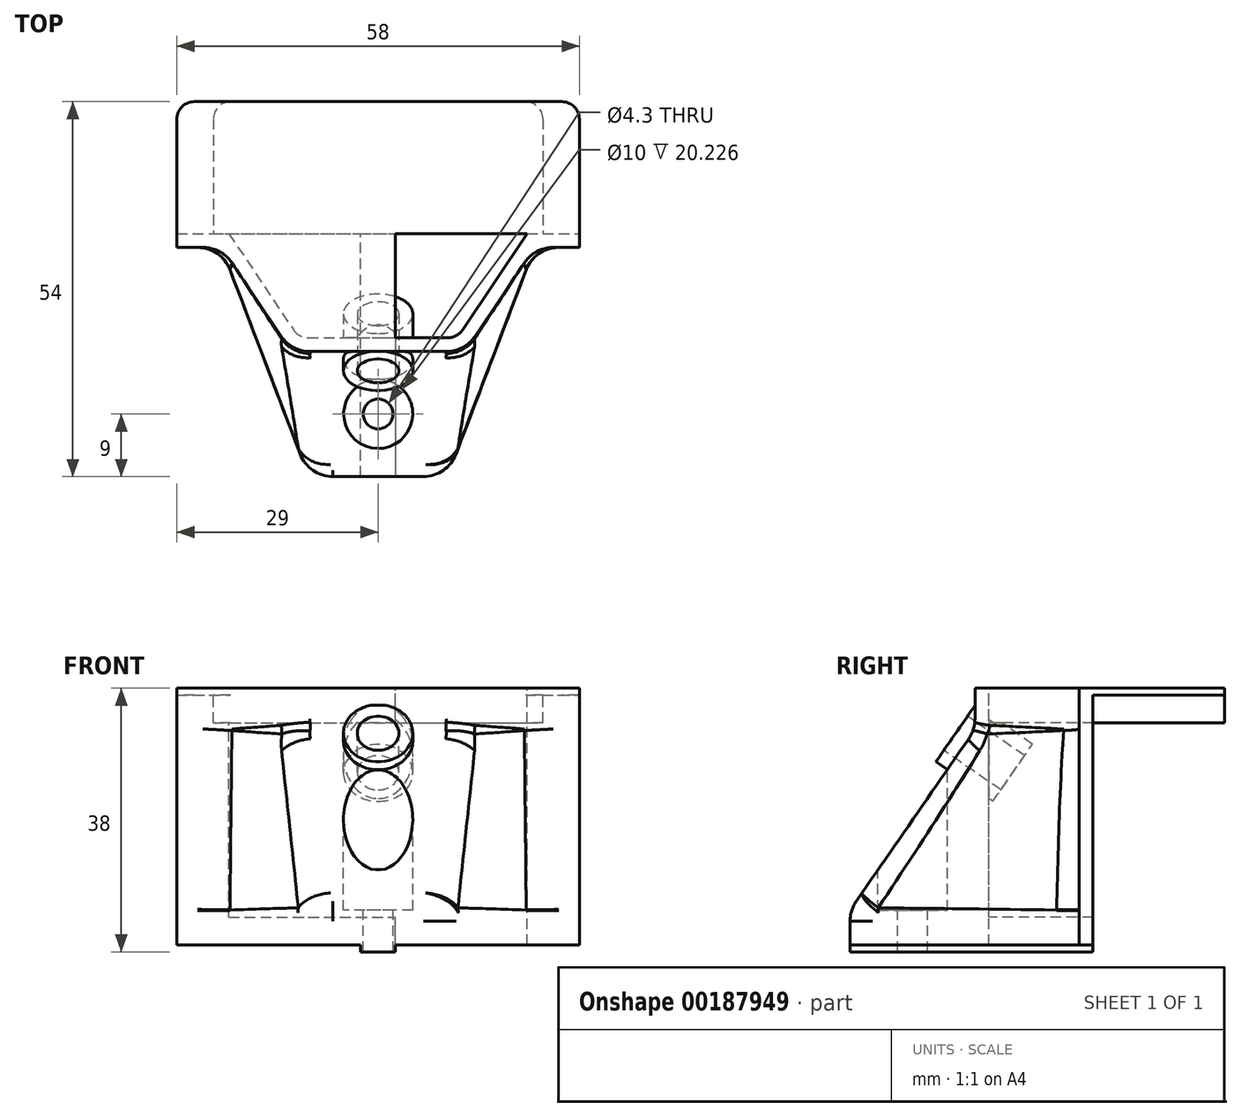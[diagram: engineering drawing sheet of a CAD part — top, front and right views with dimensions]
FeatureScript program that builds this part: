
annotation { "Feature Type Name" : "Feature", "Feature Type Description" : "" }
export const myFeature = defineFeature(function(context is Context, id is Id, definition is map)
    precondition{}
    {
        {
            var Q0;
            Q0=qCreatedBy(makeId("Top.planeOp"),FACE);
            var sketch = newSketch(context, id + "F0", { "sketchPlane" : qUnion([Q0])});
            skLineSegment(sketch, "E0", {"start": v(0, 38.36) * mm, "end": v(0, -38.36) * mm, "construction": true});
            skLineSegment(sketch, "E1.bottom", {"start": v(-29, 19) * mm, "end": v(29, 19) * mm});
            skLineSegment(sketch, "E1.top", {"start": v(-29, 0) * mm, "end": v(29, 0) * mm});
            skLineSegment(sketch, "E1.left", {"start": v(-29, 19) * mm, "end": v(-29, 0) * mm});
            skLineSegment(sketch, "E1.right", {"start": v(29, 19) * mm, "end": v(29, 0) * mm});
            skLineSegment(sketch, "E2", {"start": v(-23.75, 19) * mm, "end": v(-23.75, 0) * mm});
            skLineSegment(sketch, "E3", {"start": v(23.75, 19) * mm, "end": v(23.75, 0) * mm});
            skLineSegment(sketch, "E4.left", {"start": v(-29, 0) * mm, "end": v(-29, -2) * mm});
            skLineSegment(sketch, "E4.right", {"start": v(29, 0) * mm, "end": v(29, -2) * mm});
            skLineSegment(sketch, "E5", {"start": v(-10, -35) * mm, "end": v(10, -35) * mm});
            skLineSegment(sketch, "E6", {"start": v(-21.5, 0) * mm, "end": v(-11.43, -15) * mm});
            skLineSegment(sketch, "E7", {"start": v(11.43, -15) * mm, "end": v(21.5, 0) * mm});
            skLineSegment(sketch, "E8", {"start": v(21.5, 0) * mm, "end": v(11.43, -15) * mm});
            skLineSegment(sketch, "E9", {"start": v(-11.43, -15) * mm, "end": v(11.43, -15) * mm});
            skLineSegment(sketch, "E10", {"start": v(-29, -2) * mm, "end": v(-22.57, -2) * mm});
            skLineSegment(sketch, "E11", {"start": v(29, -2) * mm, "end": v(22.57, -2) * mm});
            skLineSegment(sketch, "E12", {"start": v(-22.57, -2) * mm, "end": v(-12.5, -17) * mm});
            skLineSegment(sketch, "E13", {"start": v(-12.5, -17) * mm, "end": v(12.5, -17) * mm});
            skLineSegment(sketch, "E14", {"start": v(12.5, -17) * mm, "end": v(22.57, -2) * mm});
            skCircle(sketch, "E15", {"center": v(0, -26) * mm, "radius": 2.15 * mm});
            skLineSegment(sketch, "E16", {"start": v(-2.5, -35) * mm, "end": v(-2.5, 0) * mm});
            skLineSegment(sketch, "E17", {"start": v(2.5, 0) * mm, "end": v(2.5, -35) * mm});
            skLineSegment(sketch, "E18", {"start": v(-22.57, -2) * mm, "end": v(-10, -35) * mm});
            skLineSegment(sketch, "E19", {"start": v(22.57, -2) * mm, "end": v(10, -35) * mm});
            skLineSegment(sketch, "E20", {"start": v(12.5, -17) * mm, "end": v(-12.5, -17) * mm});
            skSolve(sketch);
        }
        {
            var Q0;
            {var subQ1=sQuery(id+"F0.wireOp",EDGE,"E2");Q0=makeQuery(id+"F0.imprint","IMPRINT",FACE,{"disambiguationData":[TD([[makeQuery(id+"F0.imprint","IMPRINT",EDGE,{"derivedFrom":subQ1}),1.0]])]});}
            var Q1;
            {var subQ0=sQuery(id+"F0.wireOp",EDGE,"E1.left");Q1=makeQuery(id+"F0.imprint","IMPRINT",FACE,{"disambiguationData":[TD([[makeQuery(id+"F0.imprint","IMPRINT",EDGE,{"derivedFrom":subQ0}),1.0]])]});}
            var Q2;
            {var subQ0=sQuery(id+"F0.wireOp",EDGE,"E1.right");Q2=makeQuery(id+"F0.imprint","IMPRINT",FACE,{"disambiguationData":[TD([[makeQuery(id+"F0.imprint","IMPRINT",EDGE,{"derivedFrom":subQ0}),-1.0]])]});}
            var Q3;
            {var subQ5=sQuery(id+"F0.wireOp",EDGE,"E4.left");Q3=makeQuery(id+"F0.imprint","IMPRINT",FACE,{"disambiguationData":[TD([[makeQuery(id+"F0.imprint","IMPRINT",EDGE,{"derivedFrom":subQ5}),1.0]])]});}
            var Q4;
            {var subQ0=sQuery(id+"F0.wireOp",EDGE,"E6");Q4=makeQuery(id+"F0.imprint","IMPRINT",FACE,{"disambiguationData":[TD([[makeQuery(id+"F0.imprint","IMPRINT",EDGE,{"derivedFrom":subQ0}),1.0]])]});}
            var Q5;
            {var subQ0=sQuery(id+"F0.wireOp",EDGE,"E16");var subQ1=sQuery(id+"F0.wireOp",EDGE,"E1.top");var subQ2=makeQuery(id+"F0.imprint","INTERSECT",VERTEX,{"derivedFrom":[subQ1,subQ0]});Q5=makeQuery(id+"F0.imprint","IMPRINT",FACE,{"disambiguationData":[TD([[makeQuery(id+"F0.imprint","IMPRINT",EDGE,{"disambiguationData":[TD([[subQ2,-1.0]])],"derivedFrom":subQ1}),-1.0]])]});}
            var Q6;
            {var subQ0=sQuery(id+"F0.wireOp",EDGE,"E8");Q6=makeQuery(id+"F0.imprint","IMPRINT",FACE,{"disambiguationData":[TD([[makeQuery(id+"F0.imprint","IMPRINT",EDGE,{"derivedFrom":subQ0}),-1.0]])]});}
            var Q7;
            {var subQ1=sQuery(id+"F0.wireOp",EDGE,"E4.right");Q7=makeQuery(id+"F0.imprint","IMPRINT",FACE,{"disambiguationData":[TD([[makeQuery(id+"F0.imprint","IMPRINT",EDGE,{"derivedFrom":subQ1}),-1.0]])]});}
            var Q8;
            {var subQ0=sQuery(id+"F0.wireOp",EDGE,"E16");var subQ1=sQuery(id+"F0.wireOp",EDGE,"E9");var subQ2=makeQuery(id+"F0.imprint","INTERSECT",VERTEX,{"derivedFrom":[subQ1,subQ0]});Q8=makeQuery(id+"F0.imprint","IMPRINT",FACE,{"disambiguationData":[TD([[makeQuery(id+"F0.imprint","IMPRINT",EDGE,{"disambiguationData":[TD([[subQ2,-1.0]])],"derivedFrom":subQ1}),-1.0]])]});}
            var Q9;
            {var subQ7=sQuery(id+"F0.wireOp",EDGE,"CKm9zJXj-dWNc-FXDy-1bbl-akqoD4z67Doo");Q9=makeQuery(id+"F0.imprint","IMPRINT",FACE,{"disambiguationData":[TD([[makeQuery(id+"F0.imprint","IMPRINT",EDGE,{"derivedFrom":subQ7}),-1.0]])]});}
            var Q10;
            {var subQ6=sQuery(id+"F0.wireOp",EDGE,"E6");Q10=makeQuery(id+"F0.imprint","IMPRINT",FACE,{"disambiguationData":[TD([[makeQuery(id+"F0.imprint","IMPRINT",EDGE,{"derivedFrom":subQ6}),-1.0]])]});}
            var Q11;
            {var subQ5=sQuery(id+"F0.wireOp",EDGE,"E8");Q11=makeQuery(id+"F0.imprint","IMPRINT",FACE,{"disambiguationData":[TD([[makeQuery(id+"F0.imprint","IMPRINT",EDGE,{"derivedFrom":subQ5}),1.0]])]});}
            var Q12;
            {var subQ5=sQuery(id+"F0.wireOp",EDGE,"ojLpUpTn-VgTE-xdOx-HgIy-6l8KoOz5zoZN");Q12=makeQuery(id+"F0.imprint","IMPRINT",FACE,{"disambiguationData":[TD([[makeQuery(id+"F0.imprint","IMPRINT",EDGE,{"derivedFrom":subQ5}),1.0]])]});}
            extrude(context, id + "F1", {"entities" : qUnion([Q0, Q1, Q2, Q3, Q4, Q5, Q6, Q7, Q8, Q9, Q10, Q11, Q12]), "oppositeDirection" : true, "depth" : 1 * mm});
        }
        {
            var Q0;
            {var subQ1=sQuery(id+"F0.wireOp",EDGE,"E2");Q0=makeQuery(id+"F0.imprint","IMPRINT",FACE,{"disambiguationData":[TD([[makeQuery(id+"F0.imprint","IMPRINT",EDGE,{"derivedFrom":subQ1}),1.0]])]});}
            var Q1;
            {var subQ5=sQuery(id+"F0.wireOp",EDGE,"E4.left");Q1=makeQuery(id+"F0.imprint","IMPRINT",FACE,{"disambiguationData":[TD([[makeQuery(id+"F0.imprint","IMPRINT",EDGE,{"derivedFrom":subQ5}),1.0]])]});}
            var Q2;
            {var subQ1=sQuery(id+"F0.wireOp",EDGE,"E4.right");Q2=makeQuery(id+"F0.imprint","IMPRINT",FACE,{"disambiguationData":[TD([[makeQuery(id+"F0.imprint","IMPRINT",EDGE,{"derivedFrom":subQ1}),-1.0]])]});}
            var Q3;
            {var subQ0=sQuery(id+"F0.wireOp",EDGE,"E16");var subQ1=sQuery(id+"F0.wireOp",EDGE,"E9");var subQ2=makeQuery(id+"F0.imprint","INTERSECT",VERTEX,{"derivedFrom":[subQ1,subQ0]});Q3=makeQuery(id+"F0.imprint","IMPRINT",FACE,{"disambiguationData":[TD([[makeQuery(id+"F0.imprint","IMPRINT",EDGE,{"disambiguationData":[TD([[subQ2,-1.0]])],"derivedFrom":subQ1}),-1.0]])]});}
            var Q4;
            {var subQ0=sQuery(id+"F0.wireOp",EDGE,"E8");Q4=makeQuery(id+"F0.imprint","IMPRINT",FACE,{"disambiguationData":[TD([[makeQuery(id+"F0.imprint","IMPRINT",EDGE,{"derivedFrom":subQ0}),-1.0]])]});}
            var Q5;
            {var subQ0=sQuery(id+"F0.wireOp",EDGE,"E16");var subQ1=sQuery(id+"F0.wireOp",EDGE,"E1.top");var subQ2=makeQuery(id+"F0.imprint","INTERSECT",VERTEX,{"derivedFrom":[subQ1,subQ0]});Q5=makeQuery(id+"F0.imprint","IMPRINT",FACE,{"disambiguationData":[TD([[makeQuery(id+"F0.imprint","IMPRINT",EDGE,{"disambiguationData":[TD([[subQ2,-1.0]])],"derivedFrom":subQ1}),-1.0]])]});}
            var Q6;
            {var subQ0=sQuery(id+"F0.wireOp",EDGE,"E6");Q6=makeQuery(id+"F0.imprint","IMPRINT",FACE,{"disambiguationData":[TD([[makeQuery(id+"F0.imprint","IMPRINT",EDGE,{"derivedFrom":subQ0}),1.0]])]});}
            var Q7;
            {var subQ7=sQuery(id+"F0.wireOp",EDGE,"CKm9zJXj-dWNc-FXDy-1bbl-akqoD4z67Doo");Q7=makeQuery(id+"F0.imprint","IMPRINT",FACE,{"disambiguationData":[TD([[makeQuery(id+"F0.imprint","IMPRINT",EDGE,{"derivedFrom":subQ7}),-1.0]])]});}
            var Q8;
            {var subQ6=sQuery(id+"F0.wireOp",EDGE,"E6");Q8=makeQuery(id+"F0.imprint","IMPRINT",FACE,{"disambiguationData":[TD([[makeQuery(id+"F0.imprint","IMPRINT",EDGE,{"derivedFrom":subQ6}),-1.0]])]});}
            var Q9;
            {var subQ5=sQuery(id+"F0.wireOp",EDGE,"E8");Q9=makeQuery(id+"F0.imprint","IMPRINT",FACE,{"disambiguationData":[TD([[makeQuery(id+"F0.imprint","IMPRINT",EDGE,{"derivedFrom":subQ5}),1.0]])]});}
            var Q10;
            {var subQ5=sQuery(id+"F0.wireOp",EDGE,"ojLpUpTn-VgTE-xdOx-HgIy-6l8KoOz5zoZN");Q10=makeQuery(id+"F0.imprint","IMPRINT",FACE,{"disambiguationData":[TD([[makeQuery(id+"F0.imprint","IMPRINT",EDGE,{"derivedFrom":subQ5}),1.0]])]});}
            extrude(context, id + "F2", {"entities" : qUnion([Q0, Q1, Q2, Q3, Q4, Q5, Q6, Q7, Q8, Q9, Q10]), "operationType" : NewBodyOperationType.ADD, "oppositeDirection" : true, "depth" : 5 * mm, "hasSecondDirection" : true, "secondDirectionOppositeDirection" : true, "secondDirectionDepth" : 1 * mm});
        }
        {
            var Q0;
            {var subQ0=sQuery(id+"F0.wireOp",EDGE,"E16");var subQ1=sQuery(id+"F0.wireOp",EDGE,"Ah3oLFyD-nscL-xTTO-zcLj-mXIpSbA0FtKH");var subQ2=makeQuery(id+"F0.imprint","INTERSECT",VERTEX,{"disambiguationData":[OD(0.0)],"derivedFrom":[subQ1,subQ0]});Q0=makeQuery(id+"F0.imprint","IMPRINT",FACE,{"disambiguationData":[TD([[makeQuery(id+"F0.imprint","IMPRINT",EDGE,{"disambiguationData":[TD([[subQ2,-1.0]])],"derivedFrom":subQ1}),1.0]])]});}
            var Q1;
            {var subQ0=sQuery(id+"F0.wireOp",EDGE,"E16");var subQ1=sQuery(id+"F0.wireOp",EDGE,"E5");var subQ2=makeQuery(id+"F0.imprint","INTERSECT",VERTEX,{"derivedFrom":[subQ1,subQ0]});Q1=makeQuery(id+"F0.imprint","IMPRINT",FACE,{"disambiguationData":[TD([[makeQuery(id+"F0.imprint","IMPRINT",EDGE,{"disambiguationData":[TD([[subQ2,-1.0]])],"derivedFrom":subQ1}),1.0]])]});}
            var Q2;
            Q2=makeQuery(id+"F0.imprint","IMPRINT",FACE,{"disambiguationData":[TD([[makeQuery(id+"F0.imprint","IMPRINT",EDGE,{"derivedFrom":sQuery(id+"F0.wireOp",EDGE,"E15")}),-1.0]])]});
            var Q3;
            {var subQ5=sQuery(id+"F0.wireOp",EDGE,"gXHjxx1o-LBkh-gjxu-DR8X-Vu5xXttBdvo7");Q3=makeQuery(id+"F0.imprint","IMPRINT",FACE,{"disambiguationData":[TD([[makeQuery(id+"F0.imprint","IMPRINT",EDGE,{"derivedFrom":subQ5}),-1.0]])]});}
            var Q4;
            {var subQ0=sQuery(id+"F0.wireOp",EDGE,"E17");var subQ1=sQuery(id+"F0.wireOp",EDGE,"Ah3oLFyD-nscL-xTTO-zcLj-mXIpSbA0FtKH");var subQ2=makeQuery(id+"F0.imprint","INTERSECT",VERTEX,{"disambiguationData":[OD(0.0)],"derivedFrom":[subQ1,subQ0]});Q4=makeQuery(id+"F0.imprint","IMPRINT",FACE,{"disambiguationData":[TD([[makeQuery(id+"F0.imprint","IMPRINT",EDGE,{"disambiguationData":[TD([[subQ2,1.0]])],"derivedFrom":subQ1}),1.0]])]});}
            var Q5;
            {var subQ5=sQuery(id+"F0.wireOp",EDGE,"E4.left");Q5=makeQuery(id+"F0.imprint","IMPRINT",FACE,{"disambiguationData":[TD([[makeQuery(id+"F0.imprint","IMPRINT",EDGE,{"derivedFrom":subQ5}),1.0]])]});}
            var Q6;
            {var subQ0=sQuery(id+"F0.wireOp",EDGE,"E6");Q6=makeQuery(id+"F0.imprint","IMPRINT",FACE,{"disambiguationData":[TD([[makeQuery(id+"F0.imprint","IMPRINT",EDGE,{"derivedFrom":subQ0}),1.0]])]});}
            var Q7;
            {var subQ0=sQuery(id+"F0.wireOp",EDGE,"E8");Q7=makeQuery(id+"F0.imprint","IMPRINT",FACE,{"disambiguationData":[TD([[makeQuery(id+"F0.imprint","IMPRINT",EDGE,{"derivedFrom":subQ0}),-1.0]])]});}
            var Q8;
            {var subQ1=sQuery(id+"F0.wireOp",EDGE,"E4.right");Q8=makeQuery(id+"F0.imprint","IMPRINT",FACE,{"disambiguationData":[TD([[makeQuery(id+"F0.imprint","IMPRINT",EDGE,{"derivedFrom":subQ1}),-1.0]])]});}
            var Q9;
            {var subQ0=sQuery(id+"F0.wireOp",EDGE,"E16");var subQ1=sQuery(id+"F0.wireOp",EDGE,"E1.top");var subQ2=makeQuery(id+"F0.imprint","INTERSECT",VERTEX,{"derivedFrom":[subQ1,subQ0]});Q9=makeQuery(id+"F0.imprint","IMPRINT",FACE,{"disambiguationData":[TD([[makeQuery(id+"F0.imprint","IMPRINT",EDGE,{"disambiguationData":[TD([[subQ2,-1.0]])],"derivedFrom":subQ1}),-1.0]])]});}
            var Q10;
            {var subQ0=sQuery(id+"F0.wireOp",EDGE,"E16");var subQ1=sQuery(id+"F0.wireOp",EDGE,"E13");var subQ2=makeQuery(id+"F0.imprint","INTERSECT",VERTEX,{"derivedFrom":[subQ1,subQ0]});Q10=makeQuery(id+"F0.imprint","IMPRINT",FACE,{"disambiguationData":[TD([[makeQuery(id+"F0.imprint","IMPRINT",EDGE,{"disambiguationData":[TD([[subQ2,-1.0]])],"derivedFrom":subQ1}),-1.0]])]});}
            var Q11;
            {var subQ7=sQuery(id+"F0.wireOp",EDGE,"CKm9zJXj-dWNc-FXDy-1bbl-akqoD4z67Doo");Q11=makeQuery(id+"F0.imprint","IMPRINT",FACE,{"disambiguationData":[TD([[makeQuery(id+"F0.imprint","IMPRINT",EDGE,{"derivedFrom":subQ7}),-1.0]])]});}
            var Q12;
            {var subQ6=sQuery(id+"F0.wireOp",EDGE,"E6");Q12=makeQuery(id+"F0.imprint","IMPRINT",FACE,{"disambiguationData":[TD([[makeQuery(id+"F0.imprint","IMPRINT",EDGE,{"derivedFrom":subQ6}),-1.0]])]});}
            var Q13;
            {var subQ0=sQuery(id+"F0.wireOp",EDGE,"E16");var subQ1=sQuery(id+"F0.wireOp",EDGE,"E9");var subQ2=makeQuery(id+"F0.imprint","INTERSECT",VERTEX,{"derivedFrom":[subQ1,subQ0]});Q13=makeQuery(id+"F0.imprint","IMPRINT",FACE,{"disambiguationData":[TD([[makeQuery(id+"F0.imprint","IMPRINT",EDGE,{"disambiguationData":[TD([[subQ2,-1.0]])],"derivedFrom":subQ1}),-1.0]])]});}
            var Q14;
            {var subQ5=sQuery(id+"F0.wireOp",EDGE,"E8");Q14=makeQuery(id+"F0.imprint","IMPRINT",FACE,{"disambiguationData":[TD([[makeQuery(id+"F0.imprint","IMPRINT",EDGE,{"derivedFrom":subQ5}),1.0]])]});}
            var Q15;
            {var subQ1=sQuery(id+"F0.wireOp",EDGE,"E12");var subQ3=sQuery(id+"F0.wireOp",EDGE,"0NOjFGGp-TMjN-rOI9-zP1e-SuJYmJxnuehr");var subQ4=makeQuery(id+"F0.imprint","INTERSECT",VERTEX,{"derivedFrom":[subQ1,subQ3]});Q15=makeQuery(id+"F0.imprint","IMPRINT",FACE,{"disambiguationData":[TD([[makeQuery(id+"F0.imprint","IMPRINT",EDGE,{"disambiguationData":[TD([[subQ4,1.0]])],"derivedFrom":subQ1}),-1.0]])]});}
            var Q16;
            {var subQ5=sQuery(id+"F0.wireOp",EDGE,"E13");var subQ7=sQuery(id+"F0.wireOp",EDGE,"E12");var subQ8=makeQuery(id+"F0.imprint","INTERSECT",VERTEX,{"derivedFrom":[subQ7,subQ5]});Q16=makeQuery(id+"F0.imprint","IMPRINT",FACE,{"disambiguationData":[TD([[makeQuery(id+"F0.imprint","IMPRINT",EDGE,{"disambiguationData":[TD([[subQ8,1.0]])],"derivedFrom":subQ7}),-1.0]])]});}
            var Q17;
            {var subQ3=sQuery(id+"F0.wireOp",EDGE,"Ah3oLFyD-nscL-xTTO-zcLj-mXIpSbA0FtKH");var subQ9=sQuery(id+"F0.wireOp",EDGE,"E20");var subQ10=makeQuery(id+"F0.imprint","INTERSECT",VERTEX,{"disambiguationData":[OD(0.0)],"derivedFrom":[subQ3,subQ9]});Q17=makeQuery(id+"F0.imprint","IMPRINT",FACE,{"disambiguationData":[TD([[makeQuery(id+"F0.imprint","IMPRINT",EDGE,{"disambiguationData":[TD([[subQ10,-1.0]])],"derivedFrom":subQ3}),-1.0]])]});}
            var Q18;
            {var subQ0=sQuery(id+"F0.wireOp",EDGE,"E16");var subQ1=sQuery(id+"F0.wireOp",EDGE,"Ah3oLFyD-nscL-xTTO-zcLj-mXIpSbA0FtKH");var subQ2=makeQuery(id+"F0.imprint","INTERSECT",VERTEX,{"disambiguationData":[OD(1.0)],"derivedFrom":[subQ1,subQ0]});Q18=makeQuery(id+"F0.imprint","IMPRINT",FACE,{"disambiguationData":[TD([[makeQuery(id+"F0.imprint","IMPRINT",EDGE,{"disambiguationData":[TD([[subQ2,-1.0]])],"derivedFrom":subQ1}),1.0]])]});}
            var Q19;
            {var subQ0=sQuery(id+"F0.wireOp",EDGE,"E20");var subQ1=sQuery(id+"F0.wireOp",EDGE,"Ah3oLFyD-nscL-xTTO-zcLj-mXIpSbA0FtKH");var subQ2=makeQuery(id+"F0.imprint","INTERSECT",VERTEX,{"disambiguationData":[OD(0.0)],"derivedFrom":[subQ1,subQ0]});Q19=makeQuery(id+"F0.imprint","IMPRINT",FACE,{"disambiguationData":[TD([[makeQuery(id+"F0.imprint","IMPRINT",EDGE,{"disambiguationData":[TD([[subQ2,-1.0]])],"derivedFrom":subQ1}),1.0]])]});}
            var Q20;
            {var subQ0=sQuery(id+"F0.wireOp",EDGE,"E17");var subQ1=sQuery(id+"F0.wireOp",EDGE,"Ah3oLFyD-nscL-xTTO-zcLj-mXIpSbA0FtKH");var subQ2=makeQuery(id+"F0.imprint","INTERSECT",VERTEX,{"disambiguationData":[OD(1.0)],"derivedFrom":[subQ1,subQ0]});Q20=makeQuery(id+"F0.imprint","IMPRINT",FACE,{"disambiguationData":[TD([[makeQuery(id+"F0.imprint","IMPRINT",EDGE,{"disambiguationData":[TD([[subQ2,-1.0]])],"derivedFrom":subQ1}),1.0]])]});}
            var Q21;
            {var subQ5=sQuery(id+"F0.wireOp",EDGE,"E17");var subQ7=sQuery(id+"F0.wireOp",EDGE,"Ah3oLFyD-nscL-xTTO-zcLj-mXIpSbA0FtKH");var subQ8=makeQuery(id+"F0.imprint","INTERSECT",VERTEX,{"disambiguationData":[OD(1.0)],"derivedFrom":[subQ7,subQ5]});Q21=makeQuery(id+"F0.imprint","IMPRINT",FACE,{"disambiguationData":[TD([[makeQuery(id+"F0.imprint","IMPRINT",EDGE,{"disambiguationData":[TD([[subQ8,-1.0]])],"derivedFrom":subQ7}),-1.0]])]});}
            var Q22;
            {var subQ1=sQuery(id+"F0.wireOp",EDGE,"E13");var subQ9=sQuery(id+"F0.wireOp",EDGE,"E14");var subQ11=makeQuery(id+"F0.imprint","INTERSECT",VERTEX,{"derivedFrom":[subQ1,subQ9]});Q22=makeQuery(id+"F0.imprint","IMPRINT",FACE,{"disambiguationData":[TD([[makeQuery(id+"F0.imprint","IMPRINT",EDGE,{"disambiguationData":[TD([[subQ11,1.0]])],"derivedFrom":subQ1}),-1.0]])]});}
            var Q23;
            {var subQ1=sQuery(id+"F0.wireOp",EDGE,"E14");var subQ3=sQuery(id+"F0.wireOp",EDGE,"tBigfjPw-6Owl-bpDE-Yp1M-dKvZaqhM0liG");var subQ4=makeQuery(id+"F0.imprint","INTERSECT",VERTEX,{"derivedFrom":[subQ1,subQ3]});Q23=makeQuery(id+"F0.imprint","IMPRINT",FACE,{"disambiguationData":[TD([[makeQuery(id+"F0.imprint","IMPRINT",EDGE,{"disambiguationData":[TD([[subQ4,-1.0]])],"derivedFrom":subQ1}),-1.0]])]});}
            var Q24;
            {var subQ5=sQuery(id+"F0.wireOp",EDGE,"ojLpUpTn-VgTE-xdOx-HgIy-6l8KoOz5zoZN");Q24=makeQuery(id+"F0.imprint","IMPRINT",FACE,{"disambiguationData":[TD([[makeQuery(id+"F0.imprint","IMPRINT",EDGE,{"derivedFrom":subQ5}),1.0]])]});}
            var Q25;
            Q25=makeQuery(id+"F0.imprint","IMPRINT",FACE,{"disambiguationData":[TD([[makeQuery(id+"F0.imprint","IMPRINT",EDGE,{"derivedFrom":sQuery(id+"F0.wireOp",EDGE,"E15")}),1.0]])]});
            extrude(context, id + "F3", {"entities" : qUnion([Q0, Q1, Q2, Q3, Q4, Q5, Q6, Q7, Q8, Q9, Q10, Q11, Q12, Q13, Q14, Q15, Q16, Q17, Q18, Q19, Q20, Q21, Q22, Q23, Q24, Q25]), "operationType" : NewBodyOperationType.ADD, "oppositeDirection" : true, "depth" : 37 * mm, "hasSecondDirection" : true, "secondDirectionOppositeDirection" : true, "secondDirectionDepth" : 33 * mm});
        }
        {
            var Q0;
            {var subQ5=sQuery(id+"F0.wireOp",EDGE,"gXHjxx1o-LBkh-gjxu-DR8X-Vu5xXttBdvo7");Q0=makeQuery(id+"F0.imprint","IMPRINT",FACE,{"disambiguationData":[TD([[makeQuery(id+"F0.imprint","IMPRINT",EDGE,{"derivedFrom":subQ5}),-1.0]])]});}
            var Q1;
            {var subQ0=sQuery(id+"F0.wireOp",EDGE,"E16");var subQ1=sQuery(id+"F0.wireOp",EDGE,"E5");var subQ2=makeQuery(id+"F0.imprint","INTERSECT",VERTEX,{"derivedFrom":[subQ1,subQ0]});Q1=makeQuery(id+"F0.imprint","IMPRINT",FACE,{"disambiguationData":[TD([[makeQuery(id+"F0.imprint","IMPRINT",EDGE,{"disambiguationData":[TD([[subQ2,-1.0]])],"derivedFrom":subQ1}),1.0]])]});}
            var Q2;
            {var subQ0=sQuery(id+"F0.wireOp",EDGE,"E16");var subQ1=sQuery(id+"F0.wireOp",EDGE,"Ah3oLFyD-nscL-xTTO-zcLj-mXIpSbA0FtKH");var subQ2=makeQuery(id+"F0.imprint","INTERSECT",VERTEX,{"disambiguationData":[OD(1.0)],"derivedFrom":[subQ1,subQ0]});Q2=makeQuery(id+"F0.imprint","IMPRINT",FACE,{"disambiguationData":[TD([[makeQuery(id+"F0.imprint","IMPRINT",EDGE,{"disambiguationData":[TD([[subQ2,-1.0]])],"derivedFrom":subQ1}),1.0]])]});}
            var Q3;
            Q3=makeQuery(id+"F0.imprint","IMPRINT",FACE,{"disambiguationData":[TD([[makeQuery(id+"F0.imprint","IMPRINT",EDGE,{"derivedFrom":sQuery(id+"F0.wireOp",EDGE,"E15")}),-1.0]])]});
            var Q4;
            {var subQ0=sQuery(id+"F0.wireOp",EDGE,"E16");var subQ1=sQuery(id+"F0.wireOp",EDGE,"E13");var subQ2=makeQuery(id+"F0.imprint","INTERSECT",VERTEX,{"derivedFrom":[subQ1,subQ0]});Q4=makeQuery(id+"F0.imprint","IMPRINT",FACE,{"disambiguationData":[TD([[makeQuery(id+"F0.imprint","IMPRINT",EDGE,{"disambiguationData":[TD([[subQ2,-1.0]])],"derivedFrom":subQ1}),-1.0]])]});}
            var Q5;
            {var subQ0=sQuery(id+"F0.wireOp",EDGE,"E16");var subQ1=sQuery(id+"F0.wireOp",EDGE,"E9");var subQ2=makeQuery(id+"F0.imprint","INTERSECT",VERTEX,{"derivedFrom":[subQ1,subQ0]});Q5=makeQuery(id+"F0.imprint","IMPRINT",FACE,{"disambiguationData":[TD([[makeQuery(id+"F0.imprint","IMPRINT",EDGE,{"disambiguationData":[TD([[subQ2,-1.0]])],"derivedFrom":subQ1}),-1.0]])]});}
            var Q6;
            {var subQ0=sQuery(id+"F0.wireOp",EDGE,"E16");var subQ1=sQuery(id+"F0.wireOp",EDGE,"E1.top");var subQ2=makeQuery(id+"F0.imprint","INTERSECT",VERTEX,{"derivedFrom":[subQ1,subQ0]});Q6=makeQuery(id+"F0.imprint","IMPRINT",FACE,{"disambiguationData":[TD([[makeQuery(id+"F0.imprint","IMPRINT",EDGE,{"disambiguationData":[TD([[subQ2,-1.0]])],"derivedFrom":subQ1}),-1.0]])]});}
            var Q7;
            {var subQ0=sQuery(id+"F0.wireOp",EDGE,"E16");var subQ1=sQuery(id+"F0.wireOp",EDGE,"Ah3oLFyD-nscL-xTTO-zcLj-mXIpSbA0FtKH");var subQ2=makeQuery(id+"F0.imprint","INTERSECT",VERTEX,{"disambiguationData":[OD(0.0)],"derivedFrom":[subQ1,subQ0]});Q7=makeQuery(id+"F0.imprint","IMPRINT",FACE,{"disambiguationData":[TD([[makeQuery(id+"F0.imprint","IMPRINT",EDGE,{"disambiguationData":[TD([[subQ2,1.0]])],"derivedFrom":subQ1}),-1.0]])]});}
            var Q8;
            Q8=makeQuery(id+"F0.imprint","IMPRINT",FACE,{"disambiguationData":[TD([[makeQuery(id+"F0.imprint","IMPRINT",EDGE,{"derivedFrom":sQuery(id+"F0.wireOp",EDGE,"E15")}),1.0]])]});
            extrude(context, id + "F4", {"entities" : qUnion([Q0, Q1, Q2, Q3, Q4, Q5, Q6, Q7, Q8]), "operationType" : NewBodyOperationType.ADD, "oppositeDirection" : true, "depth" : 38 * mm, "hasSecondDirection" : true, "secondDirectionOppositeDirection" : true, "secondDirectionDepth" : 37 * mm});
        }
        {
            var Q0;
            {var subQ0=sQuery(id+"F0.wireOp",EDGE,"E4.left");Q0=makeQuery(id+"F0.imprint","IMPRINT",FACE,{"disambiguationData":[TD([[makeQuery(id+"F0.imprint","IMPRINT",EDGE,{"derivedFrom":subQ0}),1.0]])]});}
            var Q1;
            {var subQ7=sQuery(id+"F0.wireOp",EDGE,"CKm9zJXj-dWNc-FXDy-1bbl-akqoD4z67Doo");Q1=makeQuery(id+"F0.imprint","IMPRINT",FACE,{"disambiguationData":[TD([[makeQuery(id+"F0.imprint","IMPRINT",EDGE,{"derivedFrom":subQ7}),-1.0]])]});}
            var Q2;
            {var subQ6=sQuery(id+"F0.wireOp",EDGE,"E6");Q2=makeQuery(id+"F0.imprint","IMPRINT",FACE,{"disambiguationData":[TD([[makeQuery(id+"F0.imprint","IMPRINT",EDGE,{"derivedFrom":subQ6}),-1.0]])]});}
            var Q3;
            {var subQ0=sQuery(id+"F0.wireOp",EDGE,"E16");var subQ1=sQuery(id+"F0.wireOp",EDGE,"E9");var subQ2=makeQuery(id+"F0.imprint","INTERSECT",VERTEX,{"derivedFrom":[subQ1,subQ0]});Q3=makeQuery(id+"F0.imprint","IMPRINT",FACE,{"disambiguationData":[TD([[makeQuery(id+"F0.imprint","IMPRINT",EDGE,{"disambiguationData":[TD([[subQ2,-1.0]])],"derivedFrom":subQ1}),-1.0]])]});}
            var Q4;
            {var subQ5=sQuery(id+"F0.wireOp",EDGE,"E8");Q4=makeQuery(id+"F0.imprint","IMPRINT",FACE,{"disambiguationData":[TD([[makeQuery(id+"F0.imprint","IMPRINT",EDGE,{"derivedFrom":subQ5}),1.0]])]});}
            var Q5;
            {var subQ5=sQuery(id+"F0.wireOp",EDGE,"ojLpUpTn-VgTE-xdOx-HgIy-6l8KoOz5zoZN");Q5=makeQuery(id+"F0.imprint","IMPRINT",FACE,{"disambiguationData":[TD([[makeQuery(id+"F0.imprint","IMPRINT",EDGE,{"derivedFrom":subQ5}),1.0]])]});}
            var Q6;
            {var subQ0=sQuery(id+"F0.wireOp",EDGE,"E4.right");Q6=makeQuery(id+"F0.imprint","IMPRINT",FACE,{"disambiguationData":[TD([[makeQuery(id+"F0.imprint","IMPRINT",EDGE,{"derivedFrom":subQ0}),-1.0]])]});}
            extrude(context, id + "F5", {"entities" : qUnion([Q0, Q1, Q2, Q3, Q4, Q5, Q6]), "operationType" : NewBodyOperationType.ADD, "oppositeDirection" : true, "depth" : 6 * mm, "hasSecondDirection" : true, "secondDirectionOppositeDirection" : true, "secondDirectionDepth" : 5 * mm});
        }
        {
            var Q0;
            {var subQ0=sQuery(id+"F0.wireOp",EDGE,"E4.left");Q0=makeQuery(id+"F0.imprint","IMPRINT",FACE,{"disambiguationData":[TD([[makeQuery(id+"F0.imprint","IMPRINT",EDGE,{"derivedFrom":subQ0}),1.0]])]});}
            var Q1;
            {var subQ3=sQuery(id+"F0.wireOp",EDGE,"Ah3oLFyD-nscL-xTTO-zcLj-mXIpSbA0FtKH");var subQ9=sQuery(id+"F0.wireOp",EDGE,"E20");var subQ10=makeQuery(id+"F0.imprint","INTERSECT",VERTEX,{"disambiguationData":[OD(0.0)],"derivedFrom":[subQ3,subQ9]});Q1=makeQuery(id+"F0.imprint","IMPRINT",FACE,{"disambiguationData":[TD([[makeQuery(id+"F0.imprint","IMPRINT",EDGE,{"disambiguationData":[TD([[subQ10,-1.0]])],"derivedFrom":subQ3}),-1.0]])]});}
            var Q2;
            {var subQ0=sQuery(id+"F0.wireOp",EDGE,"E16");var subQ1=sQuery(id+"F0.wireOp",EDGE,"E5");var subQ2=makeQuery(id+"F0.imprint","INTERSECT",VERTEX,{"derivedFrom":[subQ1,subQ0]});Q2=makeQuery(id+"F0.imprint","IMPRINT",FACE,{"disambiguationData":[TD([[makeQuery(id+"F0.imprint","IMPRINT",EDGE,{"disambiguationData":[TD([[subQ2,-1.0]])],"derivedFrom":subQ1}),1.0]])]});}
            var Q3;
            {var subQ5=sQuery(id+"F0.wireOp",EDGE,"E17");var subQ7=sQuery(id+"F0.wireOp",EDGE,"Ah3oLFyD-nscL-xTTO-zcLj-mXIpSbA0FtKH");var subQ8=makeQuery(id+"F0.imprint","INTERSECT",VERTEX,{"disambiguationData":[OD(1.0)],"derivedFrom":[subQ7,subQ5]});Q3=makeQuery(id+"F0.imprint","IMPRINT",FACE,{"disambiguationData":[TD([[makeQuery(id+"F0.imprint","IMPRINT",EDGE,{"disambiguationData":[TD([[subQ8,-1.0]])],"derivedFrom":subQ7}),-1.0]])]});}
            var Q4;
            {var subQ0=sQuery(id+"F0.wireOp",EDGE,"E4.right");Q4=makeQuery(id+"F0.imprint","IMPRINT",FACE,{"disambiguationData":[TD([[makeQuery(id+"F0.imprint","IMPRINT",EDGE,{"derivedFrom":subQ0}),-1.0]])]});}
            var Q5;
            {var subQ0=sQuery(id+"F0.wireOp",EDGE,"E16");var subQ1=sQuery(id+"F0.wireOp",EDGE,"Ah3oLFyD-nscL-xTTO-zcLj-mXIpSbA0FtKH");var subQ2=makeQuery(id+"F0.imprint","INTERSECT",VERTEX,{"disambiguationData":[OD(1.0)],"derivedFrom":[subQ1,subQ0]});Q5=makeQuery(id+"F0.imprint","IMPRINT",FACE,{"disambiguationData":[TD([[makeQuery(id+"F0.imprint","IMPRINT",EDGE,{"disambiguationData":[TD([[subQ2,-1.0]])],"derivedFrom":subQ1}),1.0]])]});}
            var Q6;
            {var subQ0=sQuery(id+"F0.wireOp",EDGE,"E20");var subQ1=sQuery(id+"F0.wireOp",EDGE,"Ah3oLFyD-nscL-xTTO-zcLj-mXIpSbA0FtKH");var subQ2=makeQuery(id+"F0.imprint","INTERSECT",VERTEX,{"disambiguationData":[OD(0.0)],"derivedFrom":[subQ1,subQ0]});Q6=makeQuery(id+"F0.imprint","IMPRINT",FACE,{"disambiguationData":[TD([[makeQuery(id+"F0.imprint","IMPRINT",EDGE,{"disambiguationData":[TD([[subQ2,-1.0]])],"derivedFrom":subQ1}),1.0]])]});}
            var Q7;
            {var subQ0=sQuery(id+"F0.wireOp",EDGE,"E17");var subQ1=sQuery(id+"F0.wireOp",EDGE,"Ah3oLFyD-nscL-xTTO-zcLj-mXIpSbA0FtKH");var subQ2=makeQuery(id+"F0.imprint","INTERSECT",VERTEX,{"disambiguationData":[OD(1.0)],"derivedFrom":[subQ1,subQ0]});Q7=makeQuery(id+"F0.imprint","IMPRINT",FACE,{"disambiguationData":[TD([[makeQuery(id+"F0.imprint","IMPRINT",EDGE,{"disambiguationData":[TD([[subQ2,-1.0]])],"derivedFrom":subQ1}),1.0]])]});}
            var Q8;
            {var subQ7=sQuery(id+"F0.wireOp",EDGE,"CKm9zJXj-dWNc-FXDy-1bbl-akqoD4z67Doo");Q8=makeQuery(id+"F0.imprint","IMPRINT",FACE,{"disambiguationData":[TD([[makeQuery(id+"F0.imprint","IMPRINT",EDGE,{"derivedFrom":subQ7}),-1.0]])]});}
            var Q9;
            {var subQ1=sQuery(id+"F0.wireOp",EDGE,"E12");var subQ3=sQuery(id+"F0.wireOp",EDGE,"0NOjFGGp-TMjN-rOI9-zP1e-SuJYmJxnuehr");var subQ4=makeQuery(id+"F0.imprint","INTERSECT",VERTEX,{"derivedFrom":[subQ1,subQ3]});Q9=makeQuery(id+"F0.imprint","IMPRINT",FACE,{"disambiguationData":[TD([[makeQuery(id+"F0.imprint","IMPRINT",EDGE,{"disambiguationData":[TD([[subQ4,1.0]])],"derivedFrom":subQ1}),-1.0]])]});}
            var Q10;
            {var subQ5=sQuery(id+"F0.wireOp",EDGE,"ojLpUpTn-VgTE-xdOx-HgIy-6l8KoOz5zoZN");Q10=makeQuery(id+"F0.imprint","IMPRINT",FACE,{"disambiguationData":[TD([[makeQuery(id+"F0.imprint","IMPRINT",EDGE,{"derivedFrom":subQ5}),1.0]])]});}
            var Q11;
            {var subQ1=sQuery(id+"F0.wireOp",EDGE,"E14");var subQ3=sQuery(id+"F0.wireOp",EDGE,"tBigfjPw-6Owl-bpDE-Yp1M-dKvZaqhM0liG");var subQ4=makeQuery(id+"F0.imprint","INTERSECT",VERTEX,{"derivedFrom":[subQ1,subQ3]});Q11=makeQuery(id+"F0.imprint","IMPRINT",FACE,{"disambiguationData":[TD([[makeQuery(id+"F0.imprint","IMPRINT",EDGE,{"disambiguationData":[TD([[subQ4,-1.0]])],"derivedFrom":subQ1}),-1.0]])]});}
            var Q12;
            {var subQ0=sQuery(id+"F0.wireOp",EDGE,"E16");var subQ1=sQuery(id+"F0.wireOp",EDGE,"E9");var subQ2=makeQuery(id+"F0.imprint","INTERSECT",VERTEX,{"derivedFrom":[subQ1,subQ0]});Q12=makeQuery(id+"F0.imprint","IMPRINT",FACE,{"disambiguationData":[TD([[makeQuery(id+"F0.imprint","IMPRINT",EDGE,{"disambiguationData":[TD([[subQ2,-1.0]])],"derivedFrom":subQ1}),-1.0]])]});}
            var Q13;
            Q13=makeQuery(id+"F0.imprint","IMPRINT",FACE,{"disambiguationData":[TD([[makeQuery(id+"F0.imprint","IMPRINT",EDGE,{"derivedFrom":sQuery(id+"F0.wireOp",EDGE,"E15")}),1.0]])]});
            extrude(context, id + "F6", {"entities" : qUnion([Q0, Q1, Q2, Q3, Q4, Q5, Q6, Q7, Q8, Q9, Q10, Q11, Q12, Q13]), "operationType" : NewBodyOperationType.ADD, "oppositeDirection" : true, "depth" : 33 * mm, "hasSecondDirection" : true, "secondDirectionOppositeDirection" : true, "secondDirectionDepth" : 32 * mm});
        }
        {
            var Q0;
            Q0=makeQuery(id+"F6.opExtrude","CAP_FACE",FACE,{"disambiguationData":[OSD([sQuery(id+"F0.wireOp",EDGE,"E1.top"),sQuery(id+"F0.wireOp",EDGE,"E4.left"),sQuery(id+"F0.wireOp",EDGE,"E4.right"),sQuery(id+"F0.wireOp",EDGE,"E5"),sQuery(id+"F0.wireOp",EDGE,"E10"),sQuery(id+"F0.wireOp",EDGE,"E11"),sQuery(id+"F0.wireOp",EDGE,"E18"),sQuery(id+"F0.wireOp",EDGE,"E19"),sQuery(id+"F0.wireOp",EDGE,"tBigfjPw-6Owl-bpDE-Yp1M-dKvZaqhM0liG"),sQuery(id+"F0.wireOp",EDGE,"E20"),sQuery(id+"F0.wireOp",EDGE,"0NOjFGGp-TMjN-rOI9-zP1e-SuJYmJxnuehr")])],"isStart":true});
            var Q1;
            Q1=makeQuery(id+"F5.opExtrude","CAP_FACE",FACE,{"disambiguationData":[OSD([sQuery(id+"F0.wireOp",EDGE,"E1.top"),sQuery(id+"F0.wireOp",EDGE,"E4.left"),sQuery(id+"F0.wireOp",EDGE,"E4.right"),sQuery(id+"F0.wireOp",EDGE,"E6"),sQuery(id+"F0.wireOp",EDGE,"E8"),sQuery(id+"F0.wireOp",EDGE,"E9"),sQuery(id+"F0.wireOp",EDGE,"E10"),sQuery(id+"F0.wireOp",EDGE,"E11"),sQuery(id+"F0.wireOp",EDGE,"E12"),sQuery(id+"F0.wireOp",EDGE,"E13"),sQuery(id+"F0.wireOp",EDGE,"E14")])],"isStart":false});
            loft(context, id + "F7", {"sheetProfilesArray" : [{ "sheetProfileEntities" : qUnion([Q0]) }, { "sheetProfileEntities" : qUnion([Q1]) }]});
        }
        {
            var Q0;
            Q0=makeQuery(id+"F7.opLoft","SWEPT_FACE",FACE,{"disambiguationData":[OSD([sQuery(id+"F0.wireOp",EDGE,"E5"),sQuery(id+"F0.wireOp",EDGE,"E12"),sQuery(id+"F0.wireOp",EDGE,"E14"),sQuery(id+"F0.wireOp",EDGE,"E18"),sQuery(id+"F0.wireOp",EDGE,"E19"),sQuery(id+"F0.wireOp",EDGE,"E20")])]});
            cPlane(context, id + "F8", {"entities" : qUnion([Q0]), "cplaneType" : CPlaneType.OFFSET, "offset" : 2 * mm, "width" : 150 * mm, "height" : 150 * mm});
        }
        {
            var Q0;
            Q0=sQuery(id+"F0.wireOp",VERTEX,"E15.center");
            var Q1;
            Q1=makeQuery(id+"F7.opLoft","SWEPT_BODY",BODY,{"disambiguationData":[OSD([sQuery(id+"F0.wireOp",EDGE,"E1.top"),sQuery(id+"F0.wireOp",EDGE,"E4.left"),sQuery(id+"F0.wireOp",EDGE,"E4.right"),sQuery(id+"F0.wireOp",EDGE,"E5"),sQuery(id+"F0.wireOp",EDGE,"E6"),sQuery(id+"F0.wireOp",EDGE,"E8"),sQuery(id+"F0.wireOp",EDGE,"E9"),sQuery(id+"F0.wireOp",EDGE,"E10"),sQuery(id+"F0.wireOp",EDGE,"E11"),sQuery(id+"F0.wireOp",EDGE,"E12"),sQuery(id+"F0.wireOp",EDGE,"E13"),sQuery(id+"F0.wireOp",EDGE,"E14"),sQuery(id+"F0.wireOp",EDGE,"E18"),sQuery(id+"F0.wireOp",EDGE,"E19"),sQuery(id+"F0.wireOp",EDGE,"tBigfjPw-6Owl-bpDE-Yp1M-dKvZaqhM0liG"),sQuery(id+"F0.wireOp",EDGE,"E20"),sQuery(id+"F0.wireOp",EDGE,"0NOjFGGp-TMjN-rOI9-zP1e-SuJYmJxnuehr")])]});
            hole(context, id + "F9", {"style" : HoleStyle.SIMPLE, "endStyle" : HoleEndStyle.THROUGH, "holeDiameter" : 10 * mm, "locations" : qUnion([Q0]), "scope" : qUnion([Q1]), "isTappedThrough" : true});
        }
        {
            var Q0;
            Q0=sQuery(id+"F0.wireOp",VERTEX,"E15.center");
            var Q1;
            Q1=makeQuery(id+"F3.opExtrude","SWEPT_BODY",BODY,{"disambiguationData":[OSD([sQuery(id+"F0.wireOp",EDGE,"E1.top"),sQuery(id+"F0.wireOp",EDGE,"E4.left"),sQuery(id+"F0.wireOp",EDGE,"E4.right"),sQuery(id+"F0.wireOp",EDGE,"E5"),sQuery(id+"F0.wireOp",EDGE,"E10"),sQuery(id+"F0.wireOp",EDGE,"E11"),sQuery(id+"F0.wireOp",EDGE,"E18"),sQuery(id+"F0.wireOp",EDGE,"E19")])]});
            hole(context, id + "F10", {"style" : HoleStyle.SIMPLE, "endStyle" : HoleEndStyle.THROUGH, "holeDiameter" : 4.3 * mm, "locations" : qUnion([Q0]), "scope" : qUnion([Q1]), "isTappedThrough" : true});
        }
        {
            var Q0;
            Q0=makeQuery(id+"F1.opExtrude","SWEPT_BODY",BODY,{"disambiguationData":[OSD([sQuery(id+"F0.wireOp",EDGE,"E1.bottom"),sQuery(id+"F0.wireOp",EDGE,"E1.left"),sQuery(id+"F0.wireOp",EDGE,"E1.right"),sQuery(id+"F0.wireOp",EDGE,"E4.left"),sQuery(id+"F0.wireOp",EDGE,"E4.right"),sQuery(id+"F0.wireOp",EDGE,"E10"),sQuery(id+"F0.wireOp",EDGE,"E11"),sQuery(id+"F0.wireOp",EDGE,"E12"),sQuery(id+"F0.wireOp",EDGE,"E14"),sQuery(id+"F0.wireOp",EDGE,"E20")])]});
            var Q1;
            Q1=makeQuery(id+"F3.opExtrude","SWEPT_BODY",BODY,{"disambiguationData":[OSD([sQuery(id+"F0.wireOp",EDGE,"E1.top"),sQuery(id+"F0.wireOp",EDGE,"E4.left"),sQuery(id+"F0.wireOp",EDGE,"E4.right"),sQuery(id+"F0.wireOp",EDGE,"E5"),sQuery(id+"F0.wireOp",EDGE,"E10"),sQuery(id+"F0.wireOp",EDGE,"E11"),sQuery(id+"F0.wireOp",EDGE,"E18"),sQuery(id+"F0.wireOp",EDGE,"E19")])]});
            var Q2;
            Q2=makeQuery(id+"F7.opLoft","SWEPT_BODY",BODY,{"disambiguationData":[OSD([sQuery(id+"F0.wireOp",EDGE,"E1.top"),sQuery(id+"F0.wireOp",EDGE,"E4.left"),sQuery(id+"F0.wireOp",EDGE,"E4.right"),sQuery(id+"F0.wireOp",EDGE,"E5"),sQuery(id+"F0.wireOp",EDGE,"E6"),sQuery(id+"F0.wireOp",EDGE,"E8"),sQuery(id+"F0.wireOp",EDGE,"E9"),sQuery(id+"F0.wireOp",EDGE,"E10"),sQuery(id+"F0.wireOp",EDGE,"E11"),sQuery(id+"F0.wireOp",EDGE,"E12"),sQuery(id+"F0.wireOp",EDGE,"E14"),sQuery(id+"F0.wireOp",EDGE,"E18"),sQuery(id+"F0.wireOp",EDGE,"E19"),sQuery(id+"F0.wireOp",EDGE,"E20")])]});
            booleanBodies(context, id + "F11", {"operationType" : BooleanOperationType.UNION, "tools" : qUnion([Q0, Q1, Q2])});
        }
        {
            var Q0;
            Q0=qCreatedBy(id+"F8.planeOp",FACE);
            var sketch = newSketch(context, id + "F12", { "sketchPlane" : qUnion([Q0])});
            skCircle(sketch, "E21", {"center": v(0, -16.6) * mm, "radius": 5 * mm});
            skSolve(sketch);
        }
        {
            var Q0;
            Q0=makeQuery(id+"F12.imprint","IMPRINT",FACE,{"disambiguationData":[TD([[makeQuery(id+"F12.imprint","IMPRINT",EDGE,{"derivedFrom":sQuery(id+"F12.wireOp",EDGE,"E21")}),1.0]])]});
            extrude(context, id + "F13", {"entities" : qUnion([Q0]), "operationType" : NewBodyOperationType.ADD, "oppositeDirection" : true, "depth" : 10 * mm});
        }
        {
            var Q0;
            {var subQ0=sQuery(id+"F0.wireOp",EDGE,"E18");var subQ1=sQuery(id+"F0.wireOp",EDGE,"E12");var subQ2=sQuery(id+"F0.wireOp",EDGE,"E10");Q0=makeQuery(id+"F5.boolean.opBoolean","MERGE",EDGE,{"derivedFrom":[makeQuery(id+"F2.boolean.opBoolean","MERGE",EDGE,{"derivedFrom":[makeQuery(id+"F1.opExtrude","SWEPT_EDGE",EDGE,{"disambiguationData":[OSD([subQ2,subQ1,subQ0])]}),makeQuery(id+"F2.opExtrude","SWEPT_EDGE",EDGE,{"disambiguationData":[OSD([subQ2,subQ1,subQ0])]})]}),makeQuery(id+"F5.opExtrude","SWEPT_EDGE",EDGE,{"disambiguationData":[OSD([subQ2,subQ1,subQ0])]})]});}
            var Q1;
            Q1=makeQuery(id+"F7.opLoft","SWEPT_EDGE",EDGE,{"disambiguationData":[OSD([sQuery(id+"F0.wireOp",EDGE,"E10"),sQuery(id+"F0.wireOp",EDGE,"E12"),sQuery(id+"F0.wireOp",EDGE,"E18")])]});
            var Q2;
            {var subQ0=sQuery(id+"F0.wireOp",EDGE,"E18");var subQ1=sQuery(id+"F0.wireOp",EDGE,"E12");var subQ2=sQuery(id+"F0.wireOp",EDGE,"E10");Q2=makeQuery(id+"F6.boolean.opBoolean","MERGE",EDGE,{"derivedFrom":[makeQuery(id+"F3.opExtrude","SWEPT_EDGE",EDGE,{"disambiguationData":[OSD([subQ2,subQ1,subQ0])]}),makeQuery(id+"F6.opExtrude","SWEPT_EDGE",EDGE,{"disambiguationData":[OSD([subQ2,subQ1,subQ0])]})]});}
            var Q3;
            Q3=makeQuery(id+"F7.opLoft","SWEPT_EDGE",EDGE,{"disambiguationData":[OSD([sQuery(id+"F0.wireOp",EDGE,"E11"),sQuery(id+"F0.wireOp",EDGE,"E14"),sQuery(id+"F0.wireOp",EDGE,"E19")])]});
            var Q4;
            {var subQ0=sQuery(id+"F0.wireOp",EDGE,"E19");var subQ1=sQuery(id+"F0.wireOp",EDGE,"E14");var subQ2=sQuery(id+"F0.wireOp",EDGE,"E11");Q4=makeQuery(id+"F5.boolean.opBoolean","MERGE",EDGE,{"derivedFrom":[makeQuery(id+"F2.boolean.opBoolean","MERGE",EDGE,{"derivedFrom":[makeQuery(id+"F1.opExtrude","SWEPT_EDGE",EDGE,{"disambiguationData":[OSD([subQ2,subQ1,subQ0])]}),makeQuery(id+"F2.opExtrude","SWEPT_EDGE",EDGE,{"disambiguationData":[OSD([subQ2,subQ1,subQ0])]})]}),makeQuery(id+"F5.opExtrude","SWEPT_EDGE",EDGE,{"disambiguationData":[OSD([subQ2,subQ1,subQ0])]})]});}
            var Q5;
            {var subQ0=sQuery(id+"F0.wireOp",EDGE,"E19");var subQ1=sQuery(id+"F0.wireOp",EDGE,"E14");var subQ2=sQuery(id+"F0.wireOp",EDGE,"E11");Q5=makeQuery(id+"F6.boolean.opBoolean","MERGE",EDGE,{"derivedFrom":[makeQuery(id+"F3.opExtrude","SWEPT_EDGE",EDGE,{"disambiguationData":[OSD([subQ2,subQ1,subQ0])]}),makeQuery(id+"F6.opExtrude","SWEPT_EDGE",EDGE,{"disambiguationData":[OSD([subQ2,subQ1,subQ0])]})]});}
            var Q6;
            Q6=makeQuery(id+"F7.opLoft","SWEPT_EDGE",EDGE,{"disambiguationData":[OSD([sQuery(id+"F0.wireOp",EDGE,"E5"),sQuery(id+"F0.wireOp",EDGE,"E12"),sQuery(id+"F0.wireOp",EDGE,"E18"),sQuery(id+"F0.wireOp",EDGE,"E20")])]});
            var Q7;
            Q7=makeQuery(id+"F7.opLoft","SWEPT_EDGE",EDGE,{"disambiguationData":[OSD([sQuery(id+"F0.wireOp",EDGE,"E5"),sQuery(id+"F0.wireOp",EDGE,"E14"),sQuery(id+"F0.wireOp",EDGE,"E19"),sQuery(id+"F0.wireOp",EDGE,"E20")])]});
            var Q8;
            {var subQ0=sQuery(id+"F0.wireOp",EDGE,"E18");var subQ1=sQuery(id+"F0.wireOp",EDGE,"E5");Q8=makeQuery(id+"F6.boolean.opBoolean","MERGE",EDGE,{"derivedFrom":[makeQuery(id+"F3.opExtrude","SWEPT_EDGE",EDGE,{"disambiguationData":[OSD([subQ1,subQ0])]}),makeQuery(id+"F6.opExtrude","SWEPT_EDGE",EDGE,{"disambiguationData":[OSD([subQ1,subQ0])]})]});}
            var Q9;
            {var subQ0=sQuery(id+"F0.wireOp",EDGE,"E19");var subQ1=sQuery(id+"F0.wireOp",EDGE,"E5");Q9=makeQuery(id+"F6.boolean.opBoolean","MERGE",EDGE,{"derivedFrom":[makeQuery(id+"F3.opExtrude","SWEPT_EDGE",EDGE,{"disambiguationData":[OSD([subQ1,subQ0])]}),makeQuery(id+"F6.opExtrude","SWEPT_EDGE",EDGE,{"disambiguationData":[OSD([subQ1,subQ0])]})]});}
            var Q10;
            {var subQ0=sQuery(id+"F0.wireOp",EDGE,"E20");var subQ1=sQuery(id+"F0.wireOp",EDGE,"E14");Q10=makeQuery(id+"F5.boolean.opBoolean","MERGE",EDGE,{"derivedFrom":[makeQuery(id+"F2.boolean.opBoolean","MERGE",EDGE,{"derivedFrom":[makeQuery(id+"F1.opExtrude","SWEPT_EDGE",EDGE,{"disambiguationData":[OSD([subQ1,subQ0])]}),makeQuery(id+"F2.opExtrude","SWEPT_EDGE",EDGE,{"disambiguationData":[OSD([subQ1,subQ0])]})]}),makeQuery(id+"F5.opExtrude","SWEPT_EDGE",EDGE,{"disambiguationData":[OSD([subQ1,subQ0])]})]});}
            var Q11;
            {var subQ0=sQuery(id+"F0.wireOp",EDGE,"E20");var subQ1=sQuery(id+"F0.wireOp",EDGE,"E12");Q11=makeQuery(id+"F5.boolean.opBoolean","MERGE",EDGE,{"derivedFrom":[makeQuery(id+"F2.boolean.opBoolean","MERGE",EDGE,{"derivedFrom":[makeQuery(id+"F1.opExtrude","SWEPT_EDGE",EDGE,{"disambiguationData":[OSD([subQ1,subQ0])]}),makeQuery(id+"F2.opExtrude","SWEPT_EDGE",EDGE,{"disambiguationData":[OSD([subQ1,subQ0])]})]}),makeQuery(id+"F5.opExtrude","SWEPT_EDGE",EDGE,{"disambiguationData":[OSD([subQ1,subQ0])]})]});}
            var Q12;
            {var subQ0=sQuery(id+"F0.wireOp",EDGE,"E12");Q12=makeQuery(id+"F11.opBoolean","MERGE",EDGE,{"derivedFrom":[makeQuery(id+"F5.opExtrude","CAP_EDGE",EDGE,{"disambiguationData":[OSD([subQ0])],"isStart":false}),makeQuery(id+"F7.opLoft","MID_CAP_EDGE",EDGE,{"disambiguationData":[OSD([sQuery(id+"F0.wireOp",EDGE,"E10"),subQ0,sQuery(id+"F0.wireOp",EDGE,"E18"),sQuery(id+"F0.wireOp",EDGE,"E20")])],"capPos":1.0})]});}
            var Q13;
            {var subQ0=sQuery(id+"F0.wireOp",EDGE,"E20");Q13=makeQuery(id+"F11.opBoolean","MERGE",EDGE,{"derivedFrom":[makeQuery(id+"F5.opExtrude","CAP_EDGE",EDGE,{"disambiguationData":[OSD([subQ0])],"isStart":false}),makeQuery(id+"F7.opLoft","MID_CAP_EDGE",EDGE,{"disambiguationData":[OSD([sQuery(id+"F0.wireOp",EDGE,"E12"),sQuery(id+"F0.wireOp",EDGE,"E14"),subQ0])],"capPos":1.0})]});}
            var Q14;
            {var subQ0=sQuery(id+"F0.wireOp",EDGE,"E14");Q14=makeQuery(id+"F11.opBoolean","MERGE",EDGE,{"derivedFrom":[makeQuery(id+"F5.opExtrude","CAP_EDGE",EDGE,{"disambiguationData":[OSD([subQ0])],"isStart":false}),makeQuery(id+"F7.opLoft","MID_CAP_EDGE",EDGE,{"disambiguationData":[OSD([sQuery(id+"F0.wireOp",EDGE,"E11"),subQ0,sQuery(id+"F0.wireOp",EDGE,"E19"),sQuery(id+"F0.wireOp",EDGE,"E20")])],"capPos":1.0})]});}
            var Q15;
            {var subQ0=sQuery(id+"F0.wireOp",EDGE,"E19");Q15=makeQuery(id+"F11.opBoolean","MERGE",EDGE,{"derivedFrom":[makeQuery(id+"F6.opExtrude","CAP_EDGE",EDGE,{"disambiguationData":[OSD([subQ0])],"isStart":true}),makeQuery(id+"F7.opLoft","MID_CAP_EDGE",EDGE,{"disambiguationData":[OSD([sQuery(id+"F0.wireOp",EDGE,"E5"),sQuery(id+"F0.wireOp",EDGE,"E11"),sQuery(id+"F0.wireOp",EDGE,"E14"),subQ0])],"capPos":0.0})]});}
            var Q16;
            {var subQ0=sQuery(id+"F0.wireOp",EDGE,"E5");Q16=makeQuery(id+"F11.opBoolean","MERGE",EDGE,{"derivedFrom":[makeQuery(id+"F6.opExtrude","CAP_EDGE",EDGE,{"disambiguationData":[OSD([subQ0])],"isStart":true}),makeQuery(id+"F7.opLoft","MID_CAP_EDGE",EDGE,{"disambiguationData":[OSD([subQ0,sQuery(id+"F0.wireOp",EDGE,"E18"),sQuery(id+"F0.wireOp",EDGE,"E19")])],"capPos":0.0})]});}
            var Q17;
            {var subQ0=sQuery(id+"F0.wireOp",EDGE,"E18");Q17=makeQuery(id+"F11.opBoolean","MERGE",EDGE,{"derivedFrom":[makeQuery(id+"F6.opExtrude","CAP_EDGE",EDGE,{"disambiguationData":[OSD([subQ0])],"isStart":true}),makeQuery(id+"F7.opLoft","MID_CAP_EDGE",EDGE,{"disambiguationData":[OSD([sQuery(id+"F0.wireOp",EDGE,"E5"),sQuery(id+"F0.wireOp",EDGE,"E10"),sQuery(id+"F0.wireOp",EDGE,"E12"),subQ0])],"capPos":0.0})]});}
            fillet(context, id + "F14", {"entities" : qUnion([Q0, Q1, Q2, Q3, Q4, Q5, Q6, Q7, Q8, Q9, Q10, Q11, Q12, Q13, Q14, Q15, Q16, Q17]), "radius" : 5 * mm, "tangentPropagation" : true, "allowEdgeOverflow" : false});
        }
        {
            var Q0;
            Q0=makeQuery(id+"F5.opExtrude","CAP_EDGE",EDGE,{"disambiguationData":[OSD([sQuery(id+"F0.wireOp",EDGE,"E9")])],"isStart":true});
            var Q1;
            Q1=makeQuery(id+"F5.opExtrude","CAP_EDGE",EDGE,{"disambiguationData":[OSD([sQuery(id+"F0.wireOp",EDGE,"E8")])],"isStart":true});
            var Q2;
            {var subQ0=sQuery(id+"F0.wireOp",EDGE,"E9");var subQ1=sQuery(id+"F0.wireOp",EDGE,"E8");Q2=makeQuery(id+"F11.opBoolean","MERGE",EDGE,{"derivedFrom":[makeQuery(id+"F5.opExtrude","SWEPT_EDGE",EDGE,{"disambiguationData":[OSD([subQ1,subQ0])]}),makeQuery(id+"F6.opExtrude","SWEPT_EDGE",EDGE,{"disambiguationData":[OSD([subQ1,subQ0])]}),makeQuery(id+"F7.opLoft","SWEPT_EDGE",EDGE,{"disambiguationData":[OSD([subQ1,subQ0])]})]});}
            var Q3;
            {var subQ0=sQuery(id+"F0.wireOp",EDGE,"E9");var subQ1=sQuery(id+"F0.wireOp",EDGE,"E6");Q3=makeQuery(id+"F11.opBoolean","MERGE",EDGE,{"derivedFrom":[makeQuery(id+"F5.opExtrude","SWEPT_EDGE",EDGE,{"disambiguationData":[OSD([subQ1,subQ0])]}),makeQuery(id+"F6.opExtrude","SWEPT_EDGE",EDGE,{"disambiguationData":[OSD([subQ1,subQ0])]}),makeQuery(id+"F7.opLoft","SWEPT_EDGE",EDGE,{"disambiguationData":[OSD([subQ1,subQ0])]})]});}
            var Q4;
            Q4=makeQuery(id+"F6.opExtrude","CAP_EDGE",EDGE,{"disambiguationData":[OSD([sQuery(id+"F0.wireOp",EDGE,"E8")])],"isStart":false});
            var Q5;
            Q5=makeQuery(id+"F6.opExtrude","CAP_EDGE",EDGE,{"disambiguationData":[OSD([sQuery(id+"F0.wireOp",EDGE,"E9")])],"isStart":false});
            var Q6;
            Q6=makeQuery(id+"F6.opExtrude","CAP_EDGE",EDGE,{"disambiguationData":[OSD([sQuery(id+"F0.wireOp",EDGE,"E6")])],"isStart":false});
            var Q7;
            Q7=makeQuery(id+"F5.opExtrude","CAP_EDGE",EDGE,{"disambiguationData":[OSD([sQuery(id+"F0.wireOp",EDGE,"E6")])],"isStart":true});
            var Q8;
            Q8=makeQuery(id+"F1.opExtrude","SWEPT_EDGE",EDGE,{"disambiguationData":[OSD([sQuery(id+"F0.wireOp",EDGE,"E1.bottom"),sQuery(id+"F0.wireOp",EDGE,"E1.right")])]});
            var Q9;
            Q9=makeQuery(id+"F2.opExtrude","SWEPT_EDGE",EDGE,{"disambiguationData":[OSD([sQuery(id+"F0.wireOp",EDGE,"E1.bottom"),sQuery(id+"F0.wireOp",EDGE,"E3")])]});
            var Q10;
            Q10=makeQuery(id+"F1.opExtrude","SWEPT_EDGE",EDGE,{"disambiguationData":[OSD([sQuery(id+"F0.wireOp",EDGE,"E1.bottom"),sQuery(id+"F0.wireOp",EDGE,"E1.left")])]});
            var Q11;
            Q11=makeQuery(id+"F2.opExtrude","SWEPT_EDGE",EDGE,{"disambiguationData":[OSD([sQuery(id+"F0.wireOp",EDGE,"E1.bottom"),sQuery(id+"F0.wireOp",EDGE,"E2")])]});
            var Q12;
            Q12=makeQuery(id+"F1.opExtrude","CAP_EDGE",EDGE,{"disambiguationData":[OSD([sQuery(id+"F0.wireOp",EDGE,"E20")])],"isStart":true});
            fillet(context, id + "F15", {"entities" : qUnion([Q0, Q1, Q2, Q3, Q4, Q5, Q6, Q7, Q8, Q9, Q10, Q11, Q12]), "radius" : 2.5 * mm, "tangentPropagation" : true, "allowEdgeOverflow" : false});
        }
        {
            var Q0;
            Q0=sQuery(id+"F12.wireOp",VERTEX,"E21.center");
            var Q1;
            Q1=makeQuery(id+"F1.opExtrude","SWEPT_BODY",BODY,{"disambiguationData":[OSD([sQuery(id+"F0.wireOp",EDGE,"E1.bottom"),sQuery(id+"F0.wireOp",EDGE,"E1.left"),sQuery(id+"F0.wireOp",EDGE,"E1.right"),sQuery(id+"F0.wireOp",EDGE,"E4.left"),sQuery(id+"F0.wireOp",EDGE,"E4.right"),sQuery(id+"F0.wireOp",EDGE,"E10"),sQuery(id+"F0.wireOp",EDGE,"E11"),sQuery(id+"F0.wireOp",EDGE,"E12"),sQuery(id+"F0.wireOp",EDGE,"E14"),sQuery(id+"F0.wireOp",EDGE,"E20")])]});
            hole(context, id + "F16", {"style" : HoleStyle.SIMPLE, "endStyle" : HoleEndStyle.THROUGH, "holeDiameter" : 6 * mm, "locations" : qUnion([Q0]), "scope" : qUnion([Q1]), "isTappedThrough" : true});
        }
    });
